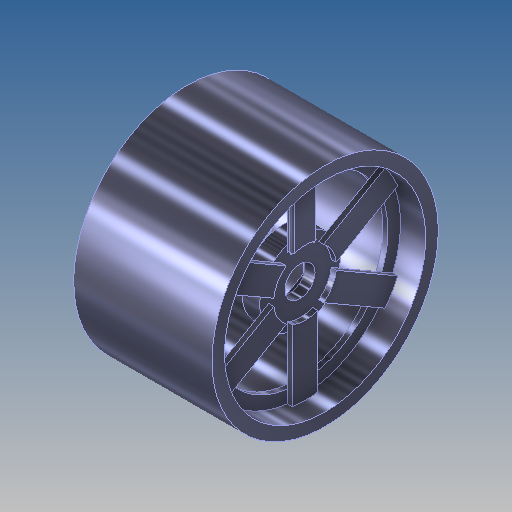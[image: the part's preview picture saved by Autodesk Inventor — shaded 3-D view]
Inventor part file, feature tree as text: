
AUTODESK INVENTOR PART (.ipt)
format: ipt  version: 2020 (Build 240168000, 168)  size: 302,592 bytes
history: native  units: mm
features: extrude x5, sketch x5, other x2, fillet x1, pattern_circular x1
ambient origin geometry x8: Origin, YZ Plane, XZ Plane, XY Plane, X Axis, Y Axis, Z Axis, Center Point
bodies: Body1 (feature_tree)
feature tree (14):
  other  "Твердое тело1"
  extrude  "Выдавливание1"  Depth=90.0mm
  other  "РабПлоскость1"
  extrude  "Выдавливание2"  Depth=5.0mm
  extrude  "Выдавливание3"  Depth=55.0mm TaperAngle=0.0deg
  extrude  "Выдавливание4"  [1 undecoded]
  fillet  "Сопряжение1"  Radius=5.0mm
  pattern_circular  "Круговой массив1"  [2 undecoded]
  extrude  "Выдавливание5"  Depth=12.0mm
  sketch  "Эскиз1"
  sketch  "Эскиз2"
  sketch  "Эскиз3"
  sketch  "Эскиз4"
  sketch  "Эскиз5"
note: 3 required parameter values undecoded (feature->parameter linkage not recoverable at this tier; creation-order binding heuristic only, values carry confidence <= 0.55)
